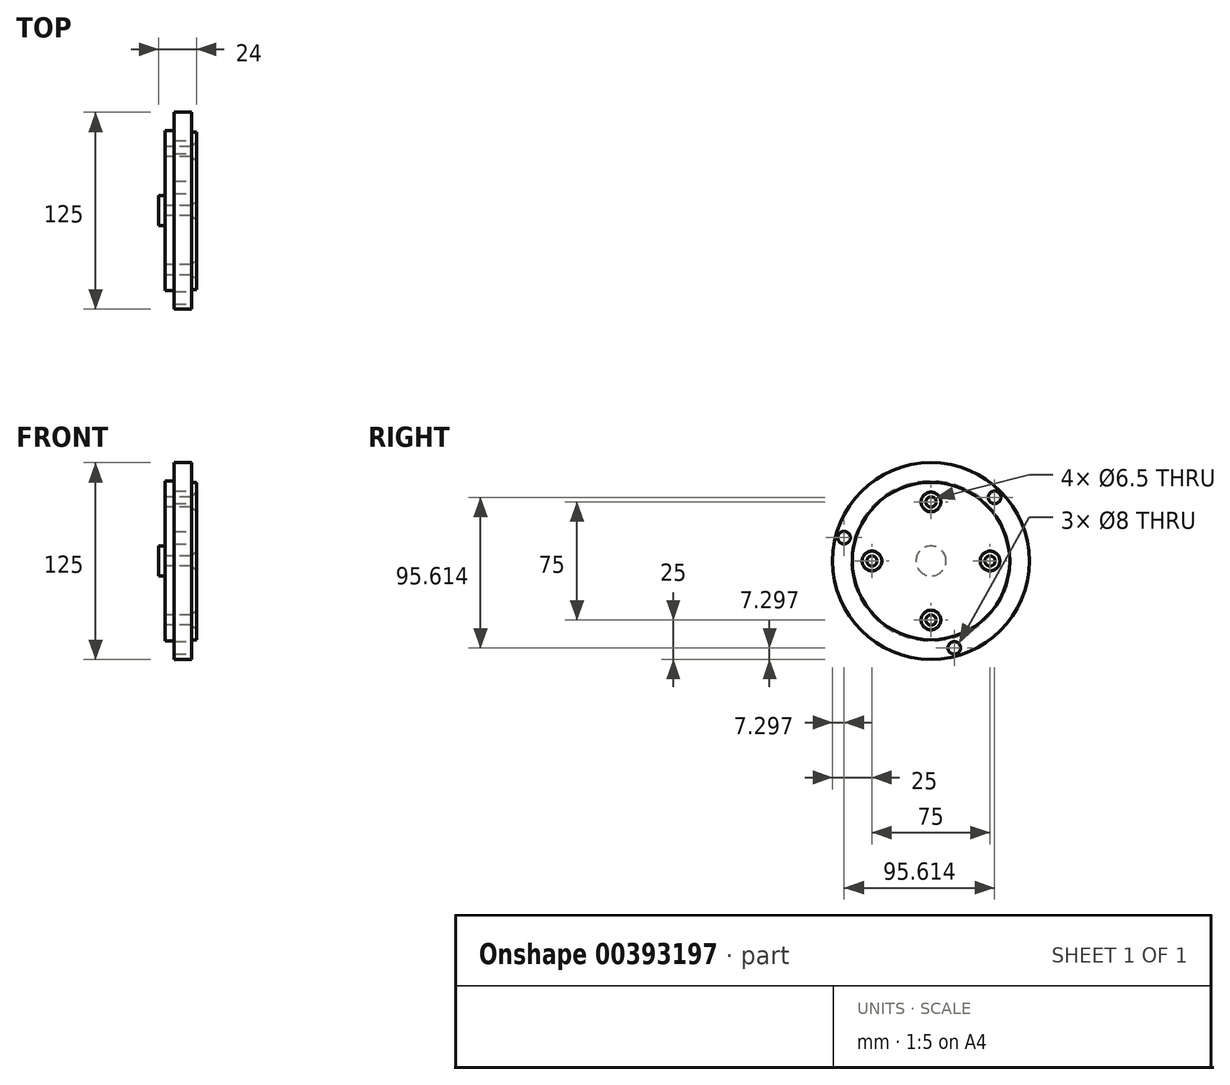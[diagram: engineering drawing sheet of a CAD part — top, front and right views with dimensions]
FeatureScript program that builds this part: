
annotation { "Feature Type Name" : "Feature", "Feature Type Description" : "" }
export const myFeature = defineFeature(function(context is Context, id is Id, definition is map)
    precondition{}
    {
        {
            var Q0;
            Q0=qCreatedBy(makeId("Front.planeOp"),FACE);
            var sketch = newSketch(context, id + "F0", { "sketchPlane" : qUnion([Q0])});
            skLineSegment(sketch, "E0", {"start": v(0, 0) * mm, "end": v(0, 9.55) * mm});
            skLineSegment(sketch, "E1", {"start": v(0, 9.55) * mm, "end": v(4, 9.55) * mm});
            skLineSegment(sketch, "E2", {"start": v(4, 9.55) * mm, "end": v(4, 50.8) * mm});
            skLineSegment(sketch, "E3", {"start": v(4, 50.8) * mm, "end": v(10, 50.8) * mm});
            skLineSegment(sketch, "E4", {"start": v(10, 50.8) * mm, "end": v(10, 62.5) * mm});
            skLineSegment(sketch, "E5", {"start": v(10, 62.5) * mm, "end": v(21, 62.5) * mm});
            skLineSegment(sketch, "E6", {"start": v(21, 62.5) * mm, "end": v(21, 50) * mm});
            skLineSegment(sketch, "E7", {"start": v(0, 0) * mm, "end": v(17.62, 0) * mm});
            skLineSegment(sketch, "E8", {"start": v(-14.05, 0) * mm, "end": v(27.4, 0) * mm});
            skLineSegment(sketch, "E9", {"start": v(21, 50) * mm, "end": v(24, 50) * mm});
            skLineSegment(sketch, "E10", {"start": v(24, 0) * mm, "end": v(24, 50) * mm});
            skSolve(sketch);
        }
        {
            var Q0;
            Q0=makeQuery(id+"F0.imprint","IMPRINT",FACE,{"disambiguationData":[TD([[makeQuery(id+"F0.imprint","IMPRINT",EDGE,{"derivedFrom":sQuery(id+"F0.wireOp",EDGE,"E0")}),-1.0]])]});
            var Q1;
            Q1=sQuery(id+"F0.wireOp",EDGE,"E7");
            revolve(context, id + "F1", {"entities" : qUnion([Q0]), "axis" : qUnion([Q1]), "revolveType" : RevolveType.FULL});
        }
        {
            var Q0;
            Q0=makeQuery(id+"F1.opRevolve","SWEPT_FACE",FACE,{"disambiguationData":[OSD([sQuery(id+"F0.wireOp",EDGE,"E6")])]});
            var sketch = newSketch(context, id + "F2", { "sketchPlane" : qUnion([Q0])});
            skLineSegment(sketch, "E11", {"start": v(0, 0) * mm, "end": v(40.41, 40.41) * mm});
            skCircle(sketch, "E12", {"center": v(40.41, 40.41) * mm, "radius": 4 * mm});
            skCircle(sketch, "E13.1.0", {"center": v(-55.2, 14.8) * mm, "radius": 4 * mm});
            skCircle(sketch, "E13.2.0", {"center": v(14.8, -55.2) * mm, "radius": 4 * mm});
            skPoint(sketch, "E13.center", {"position": v(0, 0) * mm});
            skSolve(sketch);
        }
        {
            var Q0;
            Q0=makeQuery(id+"F2.imprint","IMPRINT",FACE,{"disambiguationData":[TD([[makeQuery(id+"F2.imprint","IMPRINT",EDGE,{"derivedFrom":sQuery(id+"F2.wireOp",EDGE,"E12")}),1.0]])]});
            var Q1;
            Q1=makeQuery(id+"F2.imprint","IMPRINT",FACE,{"disambiguationData":[TD([[makeQuery(id+"F2.imprint","IMPRINT",EDGE,{"derivedFrom":sQuery(id+"F2.wireOp",EDGE,"E13.1.0")}),1.0]])]});
            var Q2;
            Q2=makeQuery(id+"F2.imprint","IMPRINT",FACE,{"disambiguationData":[TD([[makeQuery(id+"F2.imprint","IMPRINT",EDGE,{"derivedFrom":sQuery(id+"F2.wireOp",EDGE,"E13.2.0")}),1.0]])]});
            var Q3;
            Q3=makeQuery(id+"F2.imprint","IMPRINT",FACE,{"disambiguationData":[TD([[makeQuery(id+"F2.imprint","IMPRINT",EDGE,{"derivedFrom":sQuery(id+"F2.wireOp",EDGE,"E13.3.0")}),1.0]])]});
            extrude(context, id + "F3", {"entities" : qUnion([Q0, Q1, Q2, Q3]), "operationType" : NewBodyOperationType.REMOVE, "oppositeDirection" : true, "depth" : 25 * mm});
        }
        {
            var Q0;
            Q0=makeQuery(id+"F1.opRevolve","SWEPT_FACE",FACE,{"disambiguationData":[OSD([sQuery(id+"F0.wireOp",EDGE,"E2")])]});
            var sketch = newSketch(context, id + "F4", { "sketchPlane" : qUnion([Q0])});
            skPoint(sketch, "E14", {"position": v(0, 37.5) * mm});
            skCircle(sketch, "E15", {"center": v(0, 37.5) * mm, "radius": 3.25 * mm});
            skCircle(sketch, "E16.1.0", {"center": v(-37.5, 0) * mm, "radius": 3.25 * mm});
            skCircle(sketch, "E16.2.0", {"center": v(0, -37.5) * mm, "radius": 3.25 * mm});
            skCircle(sketch, "E16.3.0", {"center": v(37.5, 0) * mm, "radius": 3.25 * mm});
            skPoint(sketch, "E16.center", {"position": v(0, 0) * mm});
            skSolve(sketch);
        }
        {
            var Q0;
            Q0=makeQuery(id+"F4.imprint","IMPRINT",FACE,{"disambiguationData":[TD([[makeQuery(id+"F4.imprint","IMPRINT",EDGE,{"derivedFrom":sQuery(id+"F4.wireOp",EDGE,"E15")}),1.0]])]});
            var Q1;
            Q1=makeQuery(id+"F4.imprint","IMPRINT",FACE,{"disambiguationData":[TD([[makeQuery(id+"F4.imprint","IMPRINT",EDGE,{"derivedFrom":sQuery(id+"F4.wireOp",EDGE,"E16.1.0")}),1.0]])]});
            var Q2;
            Q2=makeQuery(id+"F4.imprint","IMPRINT",FACE,{"disambiguationData":[TD([[makeQuery(id+"F4.imprint","IMPRINT",EDGE,{"derivedFrom":sQuery(id+"F4.wireOp",EDGE,"E16.2.0")}),1.0]])]});
            var Q3;
            Q3=makeQuery(id+"F4.imprint","IMPRINT",FACE,{"disambiguationData":[TD([[makeQuery(id+"F4.imprint","IMPRINT",EDGE,{"derivedFrom":sQuery(id+"F4.wireOp",EDGE,"E16.3.0")}),1.0]])]});
            extrude(context, id + "F5", {"entities" : qUnion([Q0, Q1, Q2, Q3]), "operationType" : NewBodyOperationType.REMOVE, "oppositeDirection" : true, "depth" : 25 * mm});
        }
        {
            var Q0;
            Q0=makeQuery(id+"F5.boolean.opBoolean","INTERSECT",EDGE,{"derivedFrom":[makeQuery(id+"F1.opRevolve","SWEPT_FACE",FACE,{"disambiguationData":[OSD([sQuery(id+"F0.wireOp",EDGE,"E10")])]}),makeQuery(id+"F5.opExtrude","SWEPT_FACE",FACE,{"disambiguationData":[OSD([sQuery(id+"F4.wireOp",EDGE,"E16.3.0")])]})]});
            var Q1;
            Q1=makeQuery(id+"F5.boolean.opBoolean","INTERSECT",EDGE,{"derivedFrom":[makeQuery(id+"F1.opRevolve","SWEPT_FACE",FACE,{"disambiguationData":[OSD([sQuery(id+"F0.wireOp",EDGE,"E10")])]}),makeQuery(id+"F5.opExtrude","SWEPT_FACE",FACE,{"disambiguationData":[OSD([sQuery(id+"F4.wireOp",EDGE,"E15")])]})]});
            var Q2;
            Q2=makeQuery(id+"F5.boolean.opBoolean","INTERSECT",EDGE,{"derivedFrom":[makeQuery(id+"F1.opRevolve","SWEPT_FACE",FACE,{"disambiguationData":[OSD([sQuery(id+"F0.wireOp",EDGE,"E10")])]}),makeQuery(id+"F5.opExtrude","SWEPT_FACE",FACE,{"disambiguationData":[OSD([sQuery(id+"F4.wireOp",EDGE,"E16.1.0")])]})]});
            var Q3;
            Q3=makeQuery(id+"F5.boolean.opBoolean","INTERSECT",EDGE,{"derivedFrom":[makeQuery(id+"F1.opRevolve","SWEPT_FACE",FACE,{"disambiguationData":[OSD([sQuery(id+"F0.wireOp",EDGE,"E10")])]}),makeQuery(id+"F5.opExtrude","SWEPT_FACE",FACE,{"disambiguationData":[OSD([sQuery(id+"F4.wireOp",EDGE,"E16.2.0")])]})]});
            chamfer(context, id + "F6", {"entities" : qUnion([Q0, Q1, Q2, Q3]), "width" : 3 * mm, "tangentPropagation" : true});
        }
    });
